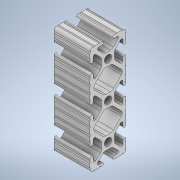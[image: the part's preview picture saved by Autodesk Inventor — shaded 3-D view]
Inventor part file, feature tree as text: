
AUTODESK INVENTOR PART (.ipt)
format: ipt  version: 2020 (Build 240168000, 168)  size: 364,544 bytes
history: native  units: in
note: dims shown in document units (in); Inventor stores cm internally (conversion verified against a paired STEP export)
features: sketch x2, extrude x1
ambient origin geometry x8: Origin, YZ Plane, XZ Plane, XY Plane, X Axis, Y Axis, Z Axis, Center Point
bodies: Solid1 (feature_tree)
feature tree (3):
  extrude  "Extrusion1"  [1 undecoded]
  sketch  "Sketch2"
  sketch  "Sketch1"  dims[d0=1.0in d1=0.0in]
note: 1 required parameter value undecoded (feature->parameter linkage not recoverable at this tier; creation-order binding heuristic only, values carry confidence <= 0.55)
